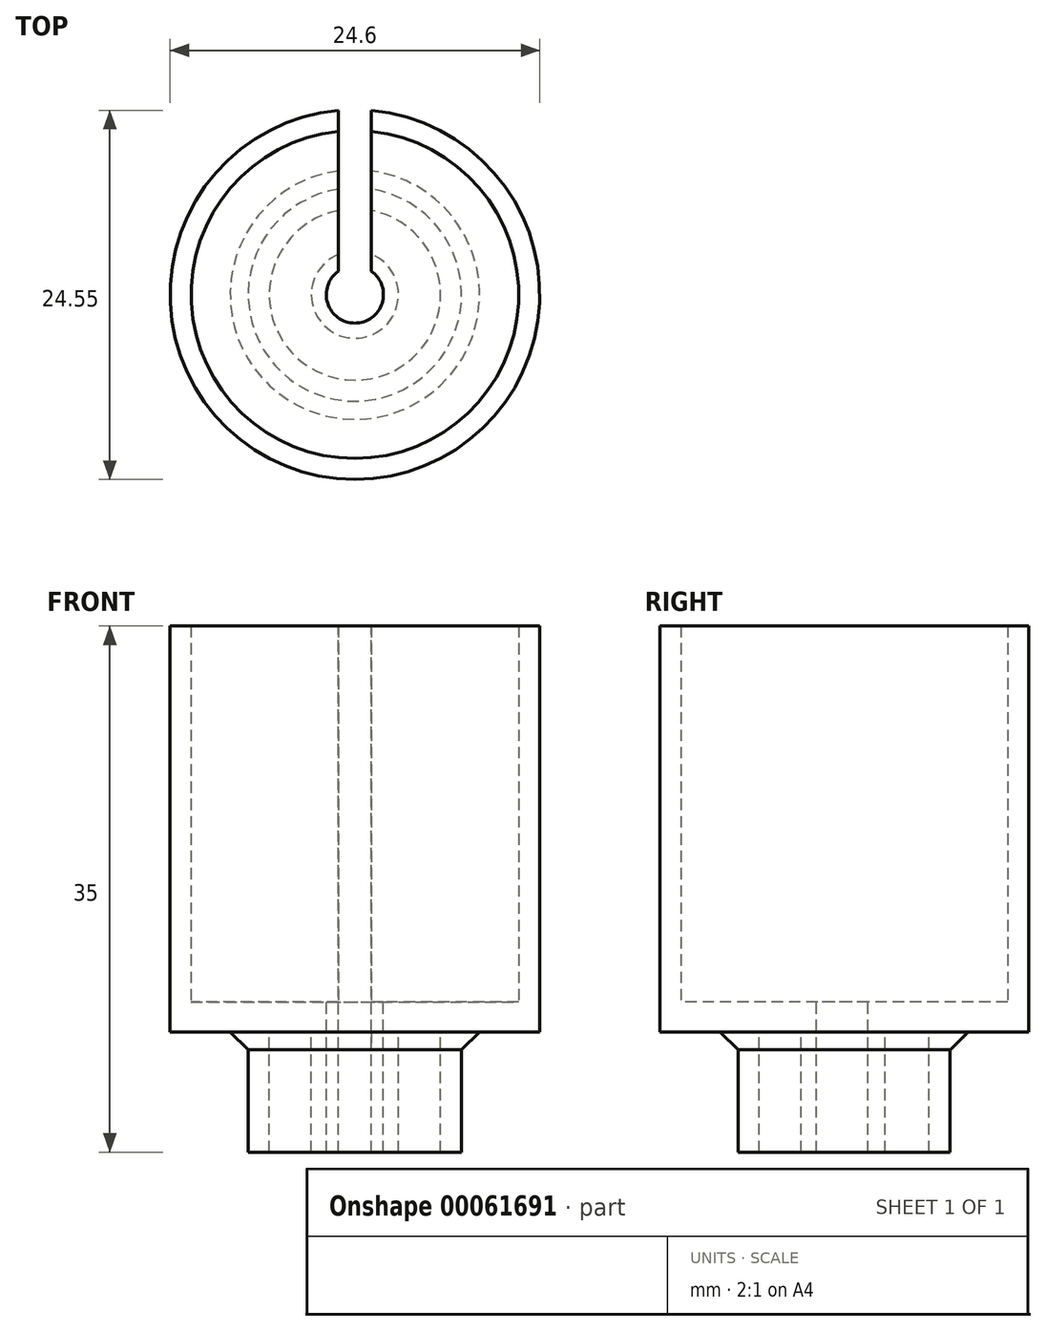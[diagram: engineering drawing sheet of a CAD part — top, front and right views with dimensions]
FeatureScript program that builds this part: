
annotation { "Feature Type Name" : "Feature", "Feature Type Description" : "" }
export const myFeature = defineFeature(function(context is Context, id is Id, definition is map)
    precondition{}
    {
        {
            var Q0;
            Q0=qCreatedBy(makeId("Top.planeOp"),FACE);
            var sketch = newSketch(context, id + "F0", { "sketchPlane" : qUnion([Q0])});
            skCircle(sketch, "E0", {"center": v(0, 0) * mm, "radius": 5.7 * mm});
            skCircle(sketch, "E1", {"center": v(0, 0) * mm, "radius": 7.1 * mm});
            skCircle(sketch, "E2", {"center": v(0, 0) * mm, "radius": 10.9 * mm});
            skCircle(sketch, "E3", {"center": v(0, 0) * mm, "radius": 12.3 * mm});
            skCircle(sketch, "E4", {"center": v(0, 0) * mm, "radius": 2.9 * mm});
            skCircle(sketch, "E5", {"center": v(0, 0) * mm, "radius": 1.9 * mm});
            skSolve(sketch);
        }
        {
            var Q0;
            Q0=makeQuery(id+"F0.imprint","IMPRINT",FACE,{"disambiguationData":[TD([[makeQuery(id+"F0.imprint","IMPRINT",EDGE,{"derivedFrom":sQuery(id+"F0.wireOp",EDGE,"E1")}),-1.0]])]});
            var Q1;
            Q1=makeQuery(id+"F0.imprint","IMPRINT",FACE,{"disambiguationData":[TD([[makeQuery(id+"F0.imprint","IMPRINT",EDGE,{"derivedFrom":sQuery(id+"F0.wireOp",EDGE,"E0")}),-1.0]])]});
            var Q2;
            Q2=makeQuery(id+"F0.imprint","IMPRINT",FACE,{"disambiguationData":[TD([[makeQuery(id+"F0.imprint","IMPRINT",EDGE,{"derivedFrom":sQuery(id+"F0.wireOp",EDGE,"E2")}),-1.0]])]});
            var Q3;
            Q3=makeQuery(id+"F0.imprint","IMPRINT",FACE,{"disambiguationData":[TD([[makeQuery(id+"F0.imprint","IMPRINT",EDGE,{"derivedFrom":sQuery(id+"F0.wireOp",EDGE,"E0")}),1.0]])]});
            var Q4;
            Q4=makeQuery(id+"F0.imprint","IMPRINT",FACE,{"disambiguationData":[TD([[makeQuery(id+"F0.imprint","IMPRINT",EDGE,{"derivedFrom":sQuery(id+"F0.wireOp",EDGE,"E4")}),1.0]])]});
            extrude(context, id + "F1", {"entities" : qUnion([Q0, Q1, Q2, Q3, Q4]), "oppositeDirection" : true, "depth" : 2 * mm, "offsetDistance" : 25 * mm});
        }
        {
            var Q0;
            Q0=makeQuery(id+"F0.imprint","IMPRINT",FACE,{"disambiguationData":[TD([[makeQuery(id+"F0.imprint","IMPRINT",EDGE,{"derivedFrom":sQuery(id+"F0.wireOp",EDGE,"E0")}),-1.0]])]});
            var Q1;
            Q1=makeQuery(id+"F0.imprint","IMPRINT",FACE,{"disambiguationData":[TD([[makeQuery(id+"F0.imprint","IMPRINT",EDGE,{"derivedFrom":sQuery(id+"F0.wireOp",EDGE,"E4")}),1.0]])]});
            extrude(context, id + "F2", {"entities" : qUnion([Q0, Q1]), "operationType" : NewBodyOperationType.ADD, "oppositeDirection" : true, "depth" : 10 * mm, "offsetDistance" : 25 * mm});
        }
        {
            var Q0;
            Q0=makeQuery(id+"F0.imprint","IMPRINT",FACE,{"disambiguationData":[TD([[makeQuery(id+"F0.imprint","IMPRINT",EDGE,{"derivedFrom":sQuery(id+"F0.wireOp",EDGE,"E2")}),-1.0]])]});
            extrude(context, id + "F3", {"entities" : qUnion([Q0]), "operationType" : NewBodyOperationType.ADD, "depth" : 25 * mm, "offsetDistance" : 25 * mm});
        }
        {
            var Q0;
            Q0=qCreatedBy(makeId("Front.planeOp"),FACE);
            var sketch = newSketch(context, id + "F4", { "sketchPlane" : qUnion([Q0])});
            skLineSegment(sketch, "E6", {"start": v(12.3, 25) * mm, "end": v(12.3, -2) * mm, "construction": true});
            skLineSegment(sketch, "E7", {"start": v(-12.3, -2) * mm, "end": v(-12.3, 25) * mm, "construction": true});
            skLineSegment(sketch, "E8", {"start": v(7.1, -2) * mm, "end": v(7.1, -8) * mm, "construction": true});
            skLineSegment(sketch, "E9", {"start": v(-7.1, -8) * mm, "end": v(-7.1, -2) * mm, "construction": true});
            skLineSegment(sketch, "E10.0", {"start": v(-7.1, -10) * mm, "end": v(7.1, -10) * mm, "construction": true});
            skLineSegment(sketch, "E11.0", {"start": v(-12.3, 25) * mm, "end": v(12.3, 25) * mm, "construction": true});
            skLineSegment(sketch, "E12", {"start": v(0, -10) * mm, "end": v(0, 25) * mm, "construction": true});
            skLineSegment(sketch, "E13.bottom", {"start": v(-1.1, 25) * mm, "end": v(1.1, 25) * mm});
            skLineSegment(sketch, "E13.top", {"start": v(-1.1, -10) * mm, "end": v(1.1, -10) * mm});
            skLineSegment(sketch, "E13.left", {"start": v(-1.1, 25) * mm, "end": v(-1.1, -10) * mm});
            skLineSegment(sketch, "E13.right", {"start": v(1.1, 25) * mm, "end": v(1.1, -10) * mm});
            skPoint(sketch, "E14", {"position": v(0, 25) * mm});
            skSolve(sketch);
        }
        {
            var Q0;
            Q0=makeQuery(id+"F4.imprint","IMPRINT",FACE,{"disambiguationData":[TD([[makeQuery(id+"F4.imprint","IMPRINT",EDGE,{"derivedFrom":sQuery(id+"F4.wireOp",EDGE,"E13.bottom")}),-1.0]])]});
            var Q1;
            {var subQ0=sQuery(id+"F0.wireOp",EDGE,"E3");Q1=makeQuery(id+"F3.boolean.opBoolean","MERGE",FACE,{"derivedFrom":[makeQuery(id+"F1.opExtrude","SWEPT_FACE",FACE,{"disambiguationData":[OSD([subQ0])]}),makeQuery(id+"F3.opExtrude","SWEPT_FACE",FACE,{"disambiguationData":[OSD([subQ0])]})]});}
            var Q2;
            Q2=makeQuery(id+"F2.opExtrude","SWEPT_BODY",BODY,{"disambiguationData":[OSD([sQuery(id+"F0.wireOp",EDGE,"E0"),sQuery(id+"F0.wireOp",EDGE,"E1")])]});
            extrude(context, id + "F5", {"entities" : qUnion([Q0]), "operationType" : NewBodyOperationType.REMOVE, "endBound" : BoundingType.THROUGH_ALL, "oppositeDirection" : true, "depth" : 25 * mm, "endBoundEntityFace" : qUnion([Q1]), "endBoundEntityBody" : qUnion([Q2]), "offsetDistance" : 25 * mm});
        }
        {
            var Q0;
            Q0=makeQuery(id+"F2.boolean.opBoolean","INTERSECT",EDGE,{"derivedFrom":[makeQuery(id+"F1.opExtrude","CAP_FACE",FACE,{"disambiguationData":[OSD([sQuery(id+"F0.wireOp",EDGE,"E3"),sQuery(id+"F0.wireOp",EDGE,"E5")])],"isStart":false}),makeQuery(id+"F2.opExtrude","SWEPT_FACE",FACE,{"disambiguationData":[OSD([sQuery(id+"F0.wireOp",EDGE,"E1")])]})]});
            chamfer(context, id + "F6", {"entities" : qUnion([Q0]), "width" : 1.2 * mm, "tangentPropagation" : true});
        }
    });
